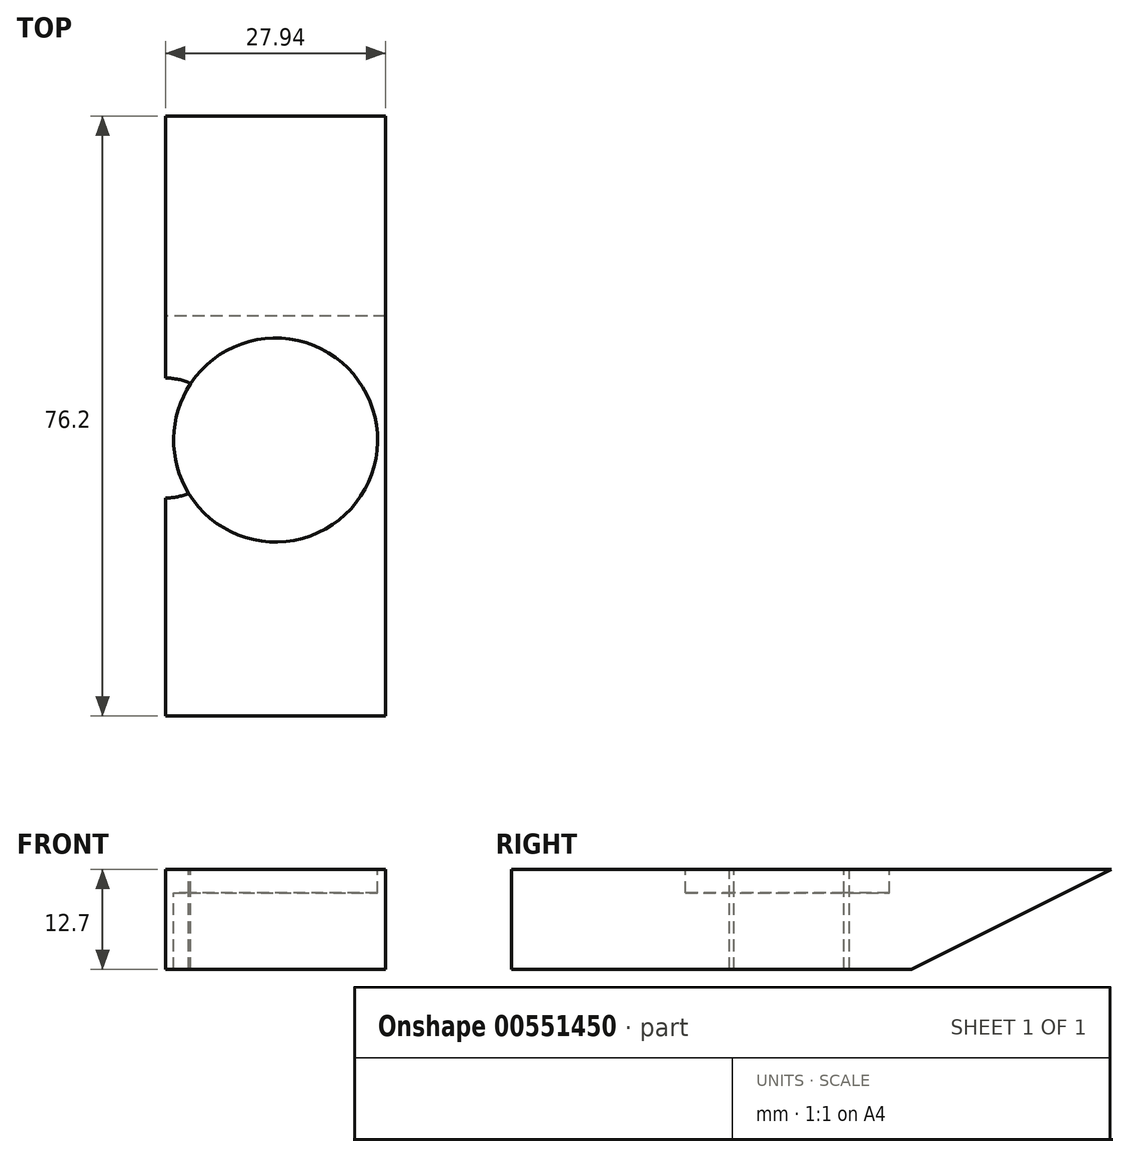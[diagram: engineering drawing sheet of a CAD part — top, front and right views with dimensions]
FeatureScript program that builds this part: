
annotation { "Feature Type Name" : "Feature", "Feature Type Description" : "" }
export const myFeature = defineFeature(function(context is Context, id is Id, definition is map)
    precondition{}
    {
        {
            var Q0;
            Q0=qCreatedBy(makeId("Right.planeOp"),FACE);
            var sketch = newSketch(context, id + "F0", { "sketchPlane" : qUnion([Q0])});
            skLineSegment(sketch, "E0", {"start": v(0, 0) * mm, "end": v(0, 12.7) * mm});
            skLineSegment(sketch, "E1", {"start": v(0, 12.7) * mm, "end": v(76.2, 12.7) * mm});
            skLineSegment(sketch, "E2", {"start": v(76.2, 12.7) * mm, "end": v(50.8, 0) * mm});
            skLineSegment(sketch, "E3", {"start": v(50.8, 0) * mm, "end": v(0, 0) * mm});
            skSolve(sketch);
        }
        {
            var Q0;
            Q0 = qSketchRegion(id + "F0", true);
            extrude(context, id + "F1", {"entities" : qUnion([Q0]), "depth" : 27.94 * mm, "offsetDistance" : 25.4 * mm});
        }
        {
            var Q0;
            Q0=makeQuery(id+"F1.opExtrude","SWEPT_FACE",FACE,{"disambiguationData":[OSD([sQuery(id+"F0.wireOp",EDGE,"E1")])]});
            var sketch = newSketch(context, id + "F2", { "sketchPlane" : qUnion([Q0])});
            skLineSegment(sketch, "E4", {"start": v(13.97, 0) * mm, "end": v(13.97, 76.2) * mm});
            skCircle(sketch, "E5", {"center": v(13.97, 35.05) * mm, "radius": 12.95 * mm});
            skLineSegment(sketch, "E6", {"start": v(13.97, 35.05) * mm, "end": v(0, 35.05) * mm, "construction": true});
            skLineSegment(sketch, "E7", {"start": v(13.97, 0) * mm, "end": v(13.97, 22.1) * mm, "construction": true});
            skLineSegment(sketch, "E8", {"start": v(13.97, 22.1) * mm, "end": v(27.94, 22.1) * mm, "construction": true});
            skLineSegment(sketch, "E9", {"start": v(13.97, 76.2) * mm, "end": v(13.97, 48) * mm, "construction": true});
            skSolve(sketch);
        }
        {
            var Q0;
            Q0 = qSketchRegion(id + "F2", true);
            extrude(context, id + "F3", {"entities" : qUnion([Q0]), "operationType" : NewBodyOperationType.REMOVE, "oppositeDirection" : true, "depth" : 3 * mm, "offsetDistance" : 25.4 * mm});
        }
        {
            var Q0;
            {var subQ4=sQuery(id+"F0.wireOp",EDGE,"E1");var subQ7=makeQuery(id+"F1.opExtrude","CAP_EDGE",EDGE,{"disambiguationData":[OSD([subQ4])],"isStart":true});Q0=makeQuery(id+"F2.imprint","IMPRINT",FACE,{"disambiguationData":[TD([[makeQuery(id+"F2.imprint","IMPRINT",EDGE,{"derivedFrom":subQ7}),-1.0]])]});}
            var sketch = newSketch(context, id + "F4", { "sketchPlane" : qUnion([Q0])});
            skLineSegment(sketch, "E10", {"start": v(0, 0) * mm, "end": v(0, 35.3) * mm, "construction": true});
            skCircle(sketch, "E11", {"center": v(0, 35.3) * mm, "radius": 7.62 * mm});
            skSolve(sketch);
        }
        {
            var Q0;
            {var subQ0=sQuery(id+"F4.wireOp",EDGE,"E11");var subQ1=makeQuery(id+"F2.imprint","IMPRINT",EDGE,{"derivedFrom":makeQuery(id+"F1.opExtrude","CAP_EDGE",EDGE,{"disambiguationData":[OSD([sQuery(id+"F0.wireOp",EDGE,"E1")])],"isStart":true})});var subQ2=makeQuery(id+"F4.imprint","INTERSECT",VERTEX,{"disambiguationData":[OD(0.0)],"derivedFrom":[subQ1,subQ0]});Q0=makeQuery(id+"F4.imprint","IMPRINT",FACE,{"disambiguationData":[TD([[makeQuery(id+"F4.imprint","IMPRINT",EDGE,{"disambiguationData":[TD([[subQ2,-1.0]])],"derivedFrom":subQ0}),1.0]])]});}
            var Q1;
            {var subQ0=sQuery(id+"F4.wireOp",EDGE,"E11");var subQ1=makeQuery(id+"F2.imprint","IMPRINT",EDGE,{"derivedFrom":makeQuery(id+"F1.opExtrude","CAP_EDGE",EDGE,{"disambiguationData":[OSD([sQuery(id+"F0.wireOp",EDGE,"E1")])],"isStart":true})});var subQ2=makeQuery(id+"F4.imprint","INTERSECT",VERTEX,{"disambiguationData":[OD(0.0)],"derivedFrom":[subQ1,subQ0]});Q1=makeQuery(id+"F4.imprint","IMPRINT",FACE,{"disambiguationData":[TD([[makeQuery(id+"F4.imprint","IMPRINT",EDGE,{"disambiguationData":[TD([[subQ2,1.0]])],"derivedFrom":subQ1}),-1.0]])]});}
            var Q2;
            {var subQ0=sQuery(id+"F4.wireOp",EDGE,"E11");var subQ1=sQuery(id+"F2.wireOp",EDGE,"E5");var subQ2=sQuery(id+"F2.wireOp",EDGE,"E4");var subQ3=makeQuery(id+"F2.imprint","IMPRINT",EDGE,{"disambiguationData":[TD([[makeQuery(id+"F2.imprint","INTERSECT",VERTEX,{"disambiguationData":[OD(0.0)],"derivedFrom":[subQ2,subQ1]}),1.0]])],"derivedFrom":subQ1});var subQ4=makeQuery(id+"F4.imprint","INTERSECT",VERTEX,{"disambiguationData":[OD(0.0)],"derivedFrom":[subQ3,subQ0]});Q2=makeQuery(id+"F4.imprint","IMPRINT",FACE,{"disambiguationData":[TD([[makeQuery(id+"F4.imprint","IMPRINT",EDGE,{"disambiguationData":[TD([[subQ4,1.0]])],"derivedFrom":subQ0}),1.0]])]});}
            extrude(context, id + "F5", {"entities" : qUnion([Q0, Q1, Q2]), "operationType" : NewBodyOperationType.REMOVE, "oppositeDirection" : true, "depth" : 25.4 * mm, "offsetDistance" : 25.4 * mm});
        }
    });
